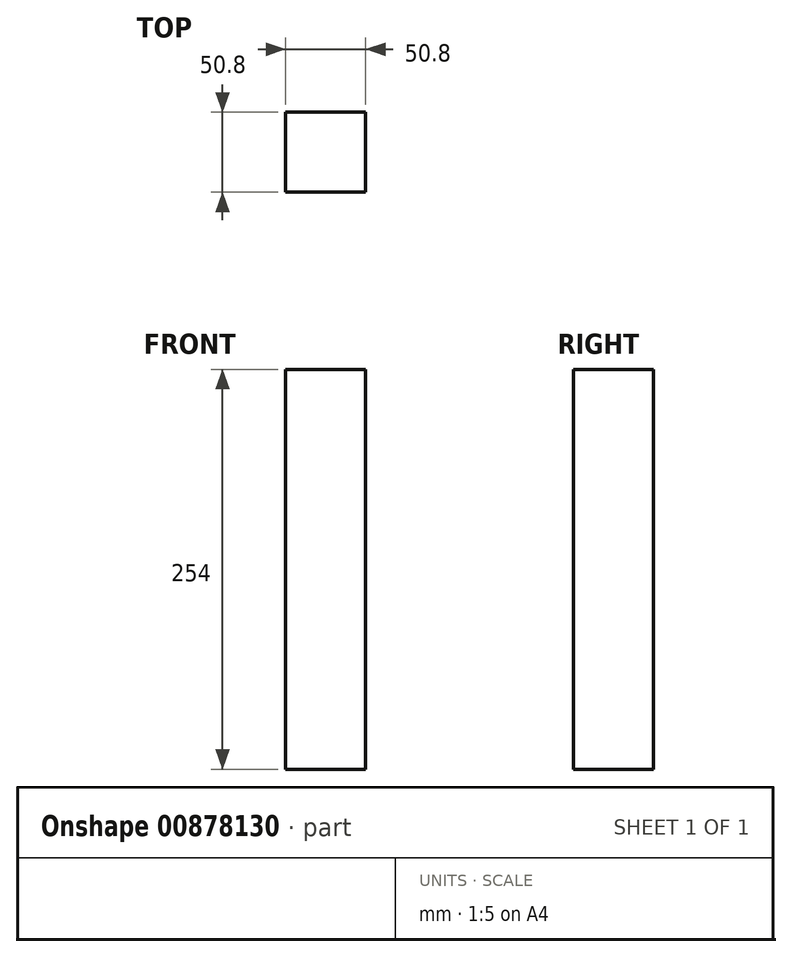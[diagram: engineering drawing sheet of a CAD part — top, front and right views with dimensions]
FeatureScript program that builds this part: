
annotation { "Feature Type Name" : "Feature", "Feature Type Description" : "" }
export const myFeature = defineFeature(function(context is Context, id is Id, definition is map)
    precondition{}
    {
        {
            var Q0;
            Q0=qCreatedBy(makeId("Top.planeOp"),FACE);
            var sketch = newSketch(context, id + "F0", { "sketchPlane" : qUnion([Q0])});
            skLineSegment(sketch, "E0.bottom", {"start": v(0, 0) * mm, "end": v(50.8, 0) * mm});
            skLineSegment(sketch, "E0.top", {"start": v(0, 50.8) * mm, "end": v(50.8, 50.8) * mm});
            skLineSegment(sketch, "E0.left", {"start": v(0, 0) * mm, "end": v(0, 50.8) * mm});
            skLineSegment(sketch, "E0.right", {"start": v(50.8, 0) * mm, "end": v(50.8, 50.8) * mm});
            skSolve(sketch);
        }
        {
            var Q0;
            Q0 = qSketchRegion(id + "F0", true);
            extrude(context, id + "F1", {"entities" : qUnion([Q0]), "depth" : 254 * mm, "offsetDistance" : 25.4 * mm});
        }
    });
